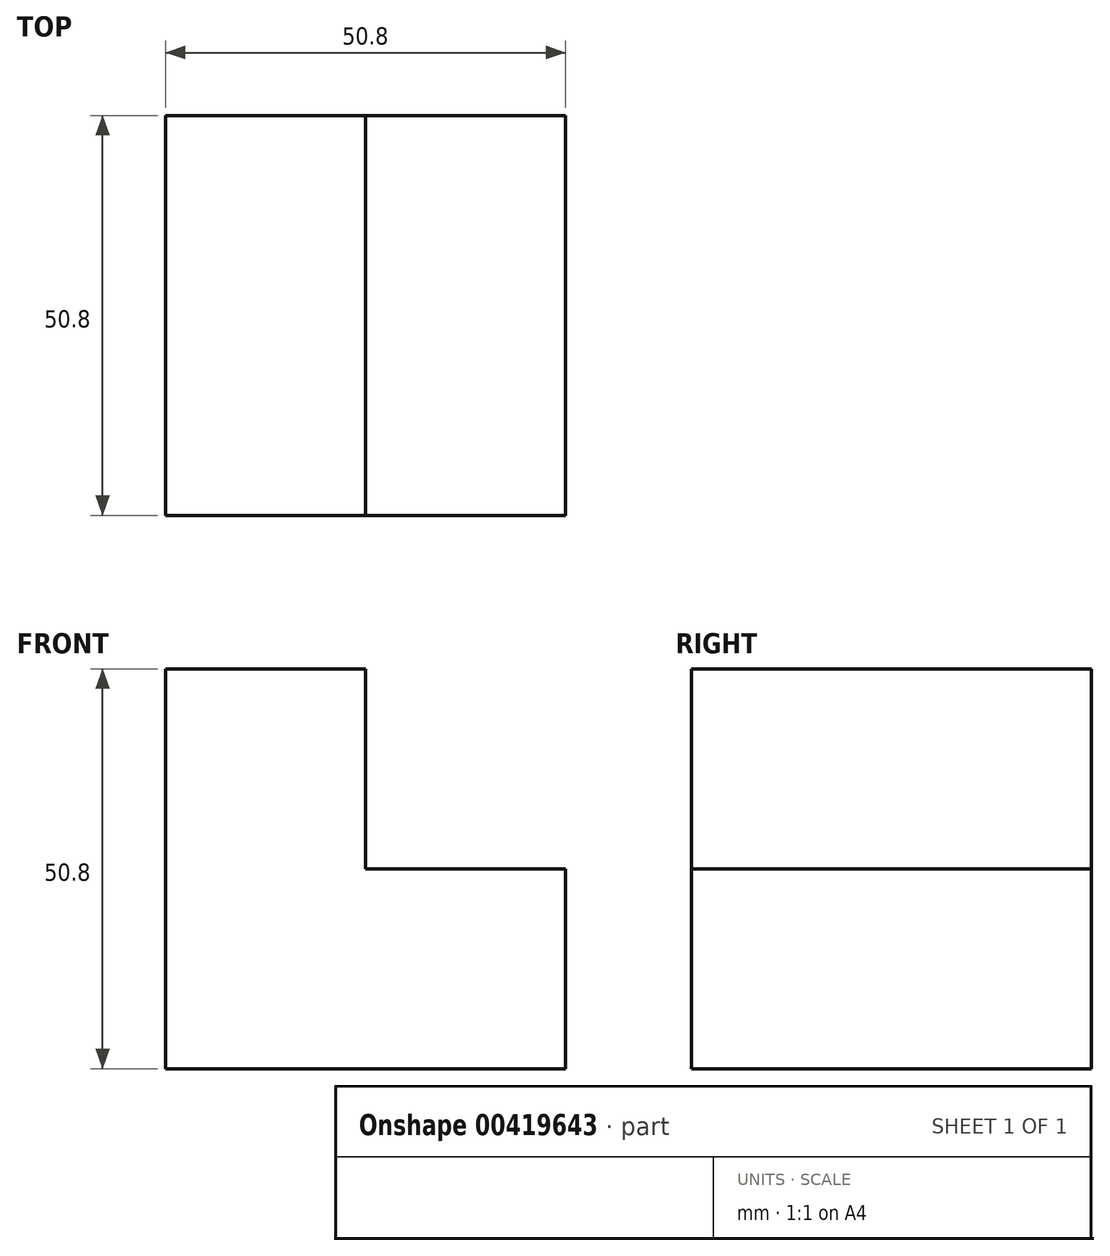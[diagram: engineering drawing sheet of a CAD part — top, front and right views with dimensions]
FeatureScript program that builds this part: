
annotation { "Feature Type Name" : "Feature", "Feature Type Description" : "" }
export const myFeature = defineFeature(function(context is Context, id is Id, definition is map)
    precondition{}
    {
        {
            var Q0;
            Q0=qCreatedBy(makeId("Front.planeOp"),FACE);
            var sketch = newSketch(context, id + "F0", { "sketchPlane" : qUnion([Q0])});
            skLineSegment(sketch, "E0", {"start": v(0, 0) * mm, "end": v(-50.8, 0) * mm});
            skLineSegment(sketch, "E1", {"start": v(-50.8, 0) * mm, "end": v(-50.8, 50.8) * mm});
            skLineSegment(sketch, "E2", {"start": v(-50.8, 50.8) * mm, "end": v(-25.4, 50.8) * mm});
            skLineSegment(sketch, "E3", {"start": v(0, 0) * mm, "end": v(0, 25.4) * mm});
            skLineSegment(sketch, "E4", {"start": v(-25.4, 50.8) * mm, "end": v(-25.4, 25.4) * mm});
            skLineSegment(sketch, "E5", {"start": v(-25.4, 25.4) * mm, "end": v(0, 25.4) * mm});
            skSolve(sketch);
        }
        {
            var Q0;
            Q0 = qSketchRegion(id + "F0", true);
            extrude(context, id + "F1", {"entities" : qUnion([Q0]), "depth" : 50.8 * mm});
        }
    });
